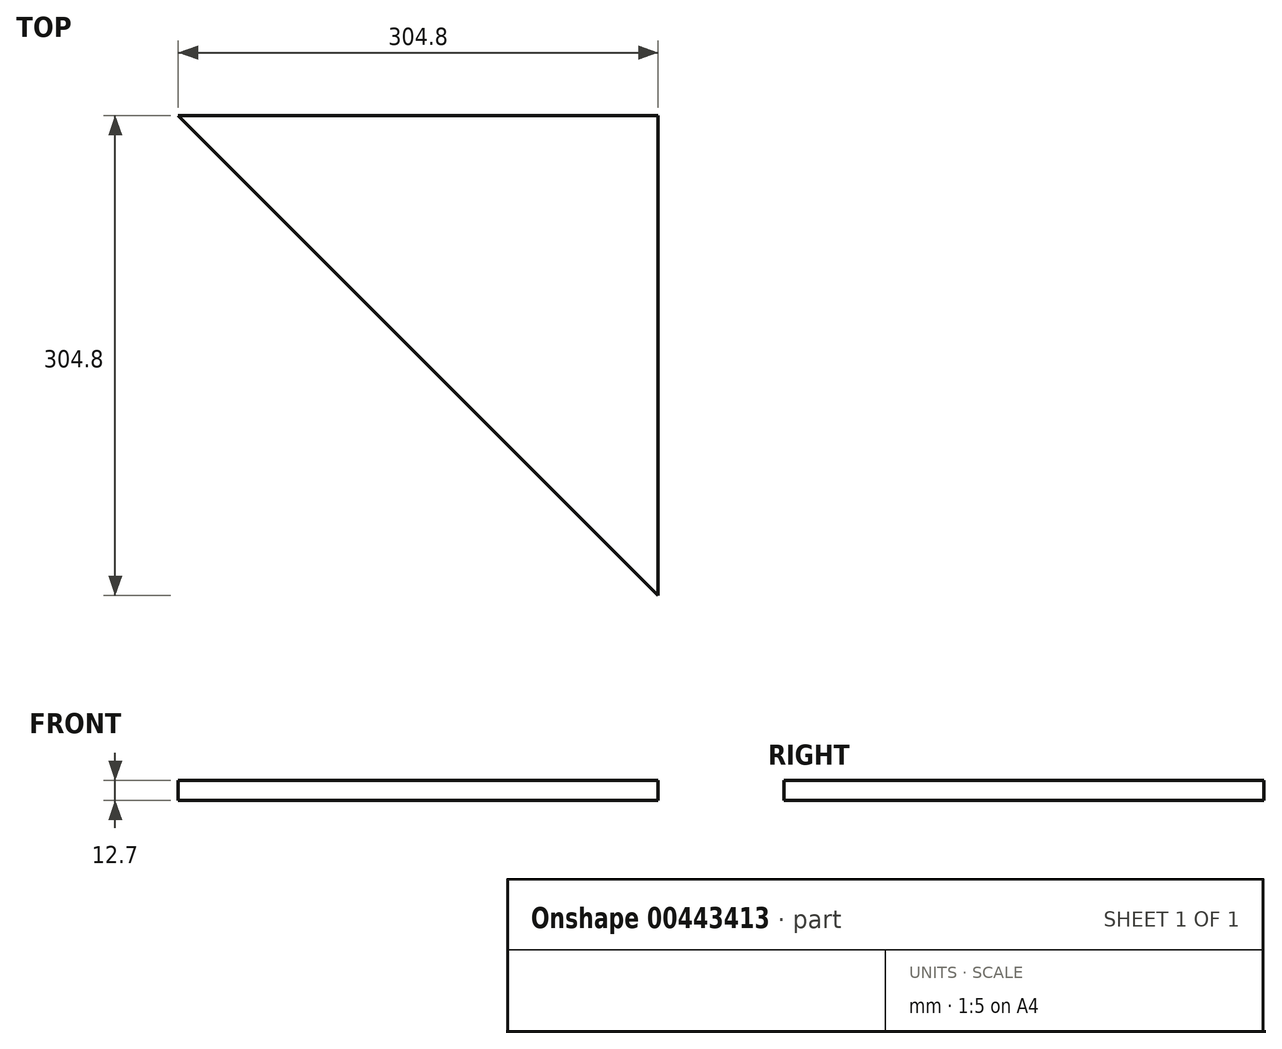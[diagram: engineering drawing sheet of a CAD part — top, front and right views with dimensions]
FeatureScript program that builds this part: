
annotation { "Feature Type Name" : "Feature", "Feature Type Description" : "" }
export const myFeature = defineFeature(function(context is Context, id is Id, definition is map)
    precondition{}
    {
        {
            var Q0;
            Q0=qCreatedBy(makeId("Top.planeOp"),FACE);
            var sketch = newSketch(context, id + "F0", { "sketchPlane" : qUnion([Q0])});
            skLineSegment(sketch, "E0", {"start": v(-154.52, 121.88) * mm, "end": v(150.28, 121.88) * mm});
            skLineSegment(sketch, "E1", {"start": v(150.28, 121.88) * mm, "end": v(150.28, -182.92) * mm});
            skLineSegment(sketch, "E2", {"start": v(150.28, -182.92) * mm, "end": v(-154.52, 121.88) * mm});
            skSolve(sketch);
        }
        {
            var Q0;
            Q0 = qSketchRegion(id + "F0", true);
            extrude(context, id + "F1", {"entities" : qUnion([Q0]), "depth" : 12.7 * mm});
        }
    });
